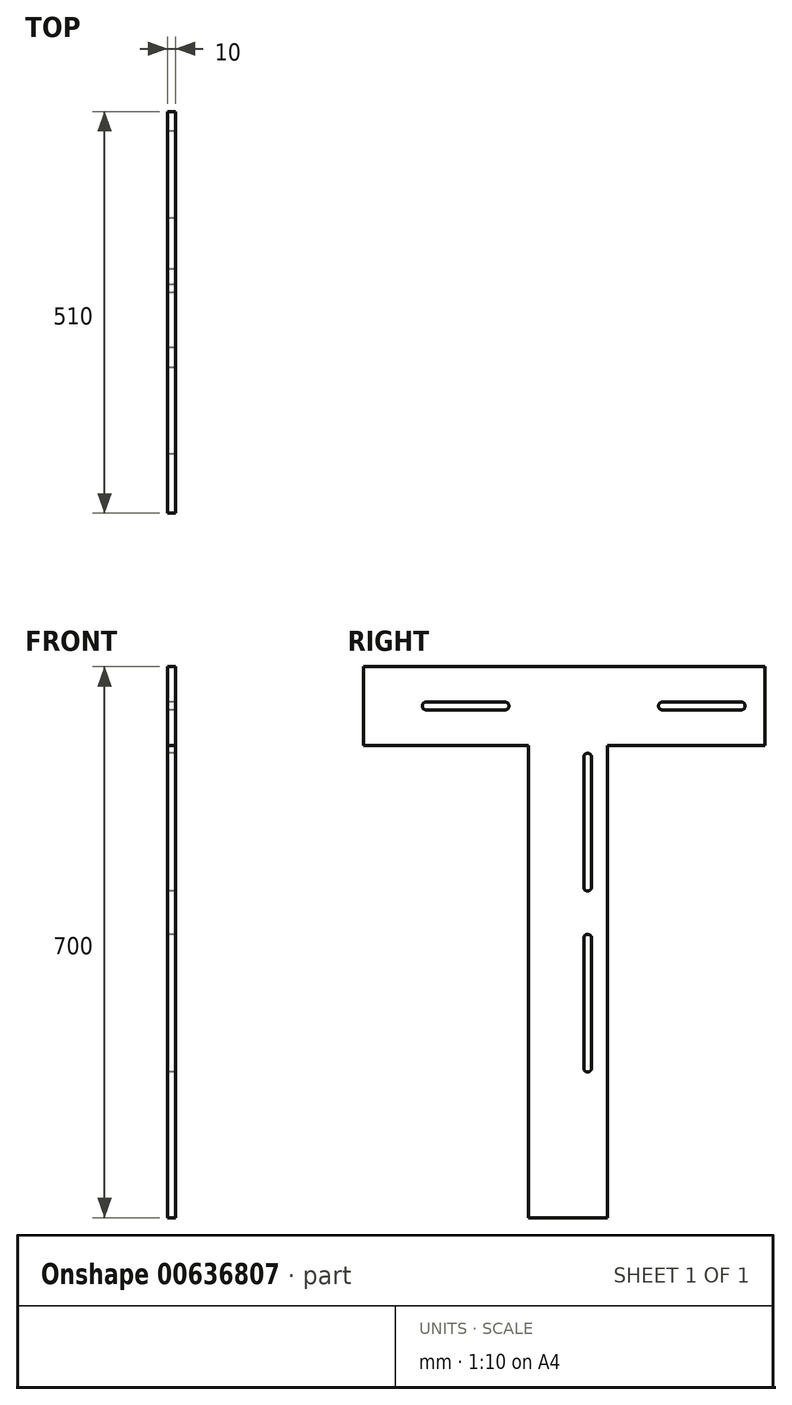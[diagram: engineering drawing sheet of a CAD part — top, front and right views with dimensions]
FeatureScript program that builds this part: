
annotation { "Feature Type Name" : "Feature", "Feature Type Description" : "" }
export const myFeature = defineFeature(function(context is Context, id is Id, definition is map)
    precondition{}
    {
        {
            var Q0;
            Q0=qCreatedBy(makeId("Right.planeOp"),FACE);
            var sketch = newSketch(context, id + "F0", { "sketchPlane" : qUnion([Q0])});
            skLineSegment(sketch, "E0.0.0", {"start": v(-57.73, -513.75) * mm, "end": v(42.27, -513.75) * mm});
            skLineSegment(sketch, "E0.0.1", {"start": v(42.27, -513.75) * mm, "end": v(42.27, 86.25) * mm});
            skLineSegment(sketch, "E0.0.2", {"start": v(42.27, 86.25) * mm, "end": v(242.27, 86.25) * mm});
            skLineSegment(sketch, "E0.0.3", {"start": v(242.27, 86.25) * mm, "end": v(242.27, 186.25) * mm});
            skLineSegment(sketch, "E0.0.4", {"start": v(242.27, 186.25) * mm, "end": v(-267.73, 186.25) * mm});
            skLineSegment(sketch, "E0.0.5", {"start": v(-267.73, 186.25) * mm, "end": v(-267.73, 86.25) * mm});
            skLineSegment(sketch, "E0.0.6", {"start": v(-267.73, 86.25) * mm, "end": v(-57.73, 86.25) * mm});
            skLineSegment(sketch, "E0.0.7", {"start": v(-57.73, 86.25) * mm, "end": v(-57.73, -513.75) * mm});
            skLineSegment(sketch, "E1.0", {"start": v(22.27, -93.75) * mm, "end": v(22.27, 71.25) * mm});
            skLineSegment(sketch, "E2", {"start": v(12.27, 71.25) * mm, "end": v(12.27, -93.75) * mm});
            skArc(sketch, "E3", {"start": v(12.27, 71.25) * mm, "mid": v(17.27, 76.25) * mm, "end": v(22.27, 71.25) * mm});
            skArc(sketch, "E4", {"start": v(12.27, -323.75) * mm, "mid": v(17.27, -328.75) * mm, "end": v(22.27, -323.75) * mm});
            skLineSegment(sketch, "E5", {"start": v(12.27, -323.75) * mm, "end": v(12.27, -158.75) * mm});
            skLineSegment(sketch, "E6.MirrorCS", {"start": v(22.27, -323.75) * mm, "end": v(22.27, -158.75) * mm});
            skArc(sketch, "E7.MirrorCS", {"start": v(12.27, -158.75) * mm, "mid": v(17.27, -153.75) * mm, "end": v(22.27, -158.75) * mm});
            skArc(sketch, "E8", {"start": v(-187.73, 141.25) * mm, "mid": v(-192.73, 136.25) * mm, "end": v(-187.73, 131.25) * mm});
            skArc(sketch, "E9", {"start": v(112.27, 141.25) * mm, "mid": v(107.27, 136.25) * mm, "end": v(112.27, 131.25) * mm});
            skArc(sketch, "E10", {"start": v(212.27, 131.25) * mm, "mid": v(217.27, 136.25) * mm, "end": v(212.27, 141.25) * mm});
            skArc(sketch, "E11", {"start": v(-87.73, 131.25) * mm, "mid": v(-82.73, 136.25) * mm, "end": v(-87.73, 141.25) * mm});
            skLineSegment(sketch, "E12", {"start": v(212.27, 141.25) * mm, "end": v(112.27, 141.25) * mm});
            skLineSegment(sketch, "E13.MirrorCS", {"start": v(212.27, 131.25) * mm, "end": v(112.27, 131.25) * mm});
            skLineSegment(sketch, "E14", {"start": v(-87.73, 141.25) * mm, "end": v(-187.73, 141.25) * mm});
            skLineSegment(sketch, "E15.MirrorCS", {"start": v(-87.73, 131.25) * mm, "end": v(-187.73, 131.25) * mm});
            skArc(sketch, "E16", {"start": v(12.27, -93.75) * mm, "mid": v(17.27, -98.75) * mm, "end": v(22.27, -93.75) * mm});
            skSolve(sketch);
        }
        {
            var Q0;
            Q0=makeQuery(id+"F0.imprint","IMPRINT",FACE,{"disambiguationData":[TD([[makeQuery(id+"F0.imprint","IMPRINT",EDGE,{"derivedFrom":sQuery(id+"F0.wireOp",EDGE,"E0.0.0")}),1.0]])]});
            extrude(context, id + "F1", {"entities" : qUnion([Q0]), "depth" : 10 * mm, "offsetDistance" : 25 * mm});
        }
    });
